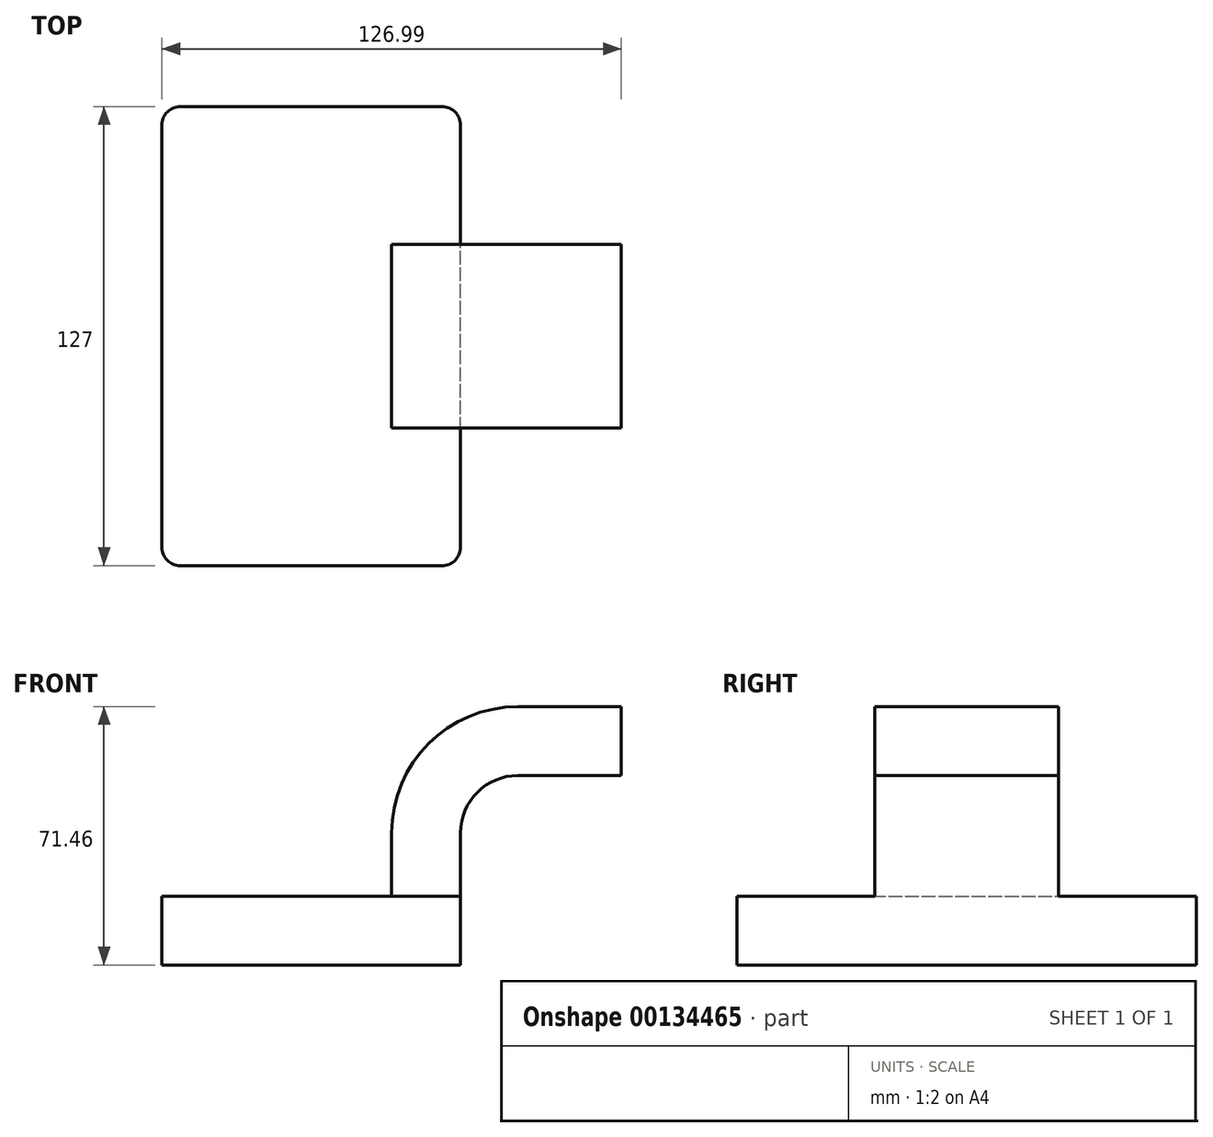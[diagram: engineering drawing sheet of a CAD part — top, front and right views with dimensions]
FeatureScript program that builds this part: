
annotation { "Feature Type Name" : "Feature", "Feature Type Description" : "" }
export const myFeature = defineFeature(function(context is Context, id is Id, definition is map)
    precondition{}
    {
        {
            var Q0;
            Q0=qCreatedBy(makeId("Front.planeOp"),FACE);
            var sketch = newSketch(context, id + "F0", { "sketchPlane" : qUnion([Q0])});
            skLineSegment(sketch, "E0.bottom", {"start": v(-41.28, -9.53) * mm, "end": v(41.28, -9.53) * mm});
            skLineSegment(sketch, "E0.top", {"start": v(-41.28, 9.53) * mm, "end": v(41.28, 9.53) * mm});
            skLineSegment(sketch, "E0.left", {"start": v(-41.28, -9.53) * mm, "end": v(-41.28, 9.53) * mm});
            skLineSegment(sketch, "E0.right", {"start": v(41.28, -9.53) * mm, "end": v(41.28, 9.53) * mm});
            skPoint(sketch, "E0.middle", {"position": v(0, 0) * mm});
            skLineSegment(sketch, "E1.bottom", {"start": v(60.32, 38.1) * mm, "end": v(111.12, 38.1) * mm});
            skLineSegment(sketch, "E1.top", {"start": v(60.32, 66.67) * mm, "end": v(111.12, 66.67) * mm});
            skLineSegment(sketch, "E1.left", {"start": v(60.32, 38.1) * mm, "end": v(60.32, 66.67) * mm});
            skLineSegment(sketch, "E1.right", {"start": v(111.12, 38.1) * mm, "end": v(111.12, 66.67) * mm});
            skPoint(sketch, "E1.middle", {"position": v(85.72, 52.39) * mm});
            skLineSegment(sketch, "E2", {"start": v(41.28, 9.52) * mm, "end": v(41.28, 27) * mm});
            skArc(sketch, "E3", {"start": v(41.27, 27) * mm, "mid": v(45.92, 38.23) * mm, "end": v(57.15, 42.88) * mm});
            skLineSegment(sketch, "E4", {"start": v(57.15, 42.88) * mm, "end": v(85.72, 42.88) * mm});
            skPoint(sketch, "E4.endSnap0", {"position": v(85.72, 38.1) * mm});
            skLineSegment(sketch, "E5.0", {"start": v(57.15, 61.93) * mm, "end": v(85.72, 61.93) * mm});
            skArc(sketch, "E5.1", {"start": v(22.22, 27) * mm, "mid": v(32.45, 51.7) * mm, "end": v(57.15, 61.93) * mm});
            skLineSegment(sketch, "E5.2", {"start": v(22.22, 9.52) * mm, "end": v(22.22, 27) * mm});
            skLineSegment(sketch, "E6", {"start": v(85.72, 42.88) * mm, "end": v(85.72, 61.93) * mm});
            skFitSpline(sketch, "E7", {"points": [v(-41.28, 9.52) * mm, v(57.15, 61.93) * mm], "startDerivative": vector(1.46, 108.1) * mm, "endDerivative": vector(105.27, -46.52) * mm});
            skSolve(sketch);
        }
        {
            var Q0;
            Q0=makeQuery(id+"F0.imprint","IMPRINT",FACE,{"disambiguationData":[TD([[makeQuery(id+"F0.imprint","IMPRINT",EDGE,{"derivedFrom":sQuery(id+"F0.wireOp",EDGE,"E0.bottom")}),1.0]])]});
            extrude(context, id + "F1", {"entities" : qUnion([Q0]), "endBound" : BoundingType.SYMMETRIC, "depth" : 127 * mm});
        }
        {
            var Q0;
            {var subQ1=sQuery(id+"F0.wireOp",EDGE,"E2");Q0=makeQuery(id+"F0.imprint","IMPRINT",FACE,{"disambiguationData":[TD([[makeQuery(id+"F0.imprint","IMPRINT",EDGE,{"derivedFrom":subQ1}),1.0]])]});}
            var Q1;
            {var subQ5=sQuery(id+"F0.wireOp",EDGE,"E6");Q1=makeQuery(id+"F0.imprint","IMPRINT",FACE,{"disambiguationData":[TD([[makeQuery(id+"F0.imprint","IMPRINT",EDGE,{"derivedFrom":subQ5}),1.0]])]});}
            extrude(context, id + "F2", {"entities" : qUnion([Q0, Q1]), "operationType" : NewBodyOperationType.ADD, "endBound" : BoundingType.SYMMETRIC, "depth" : 50.8 * mm});
        }
        {
            var Q0;
            Q0=makeQuery(id+"F0.imprint","IMPRINT",FACE,{"disambiguationData":[TD([[makeQuery(id+"F0.imprint","IMPRINT",EDGE,{"derivedFrom":sQuery(id+"F0.wireOp",EDGE,"E5.1")}),1.0]])]});
            extrude(context, id + "F3", {"entities" : qUnion([Q0]), "operationType" : NewBodyOperationType.ADD, "endBound" : BoundingType.SYMMETRIC, "depth" : 15.88 * mm});
        }
        {
            var Q0;
            Q0=makeQuery(id+"F1.opExtrude","CAP_EDGE",EDGE,{"disambiguationData":[OSD([sQuery(id+"F0.wireOp",EDGE,"E0.right")])],"isStart":false});
            var Q1;
            Q1=makeQuery(id+"F1.opExtrude","CAP_EDGE",EDGE,{"disambiguationData":[OSD([sQuery(id+"F0.wireOp",EDGE,"E0.left")])],"isStart":false});
            var Q2;
            Q2=makeQuery(id+"F1.opExtrude","CAP_EDGE",EDGE,{"disambiguationData":[OSD([sQuery(id+"F0.wireOp",EDGE,"E0.right")])],"isStart":true});
            var Q3;
            Q3=makeQuery(id+"F1.opExtrude","CAP_EDGE",EDGE,{"disambiguationData":[OSD([sQuery(id+"F0.wireOp",EDGE,"E0.left")])],"isStart":true});
            fillet(context, id + "F4", {"entities" : qUnion([Q0, Q1, Q2, Q3]), "radius" : 5.08 * mm, "tangentPropagation" : true, "allowEdgeOverflow" : false});
        }
    });
